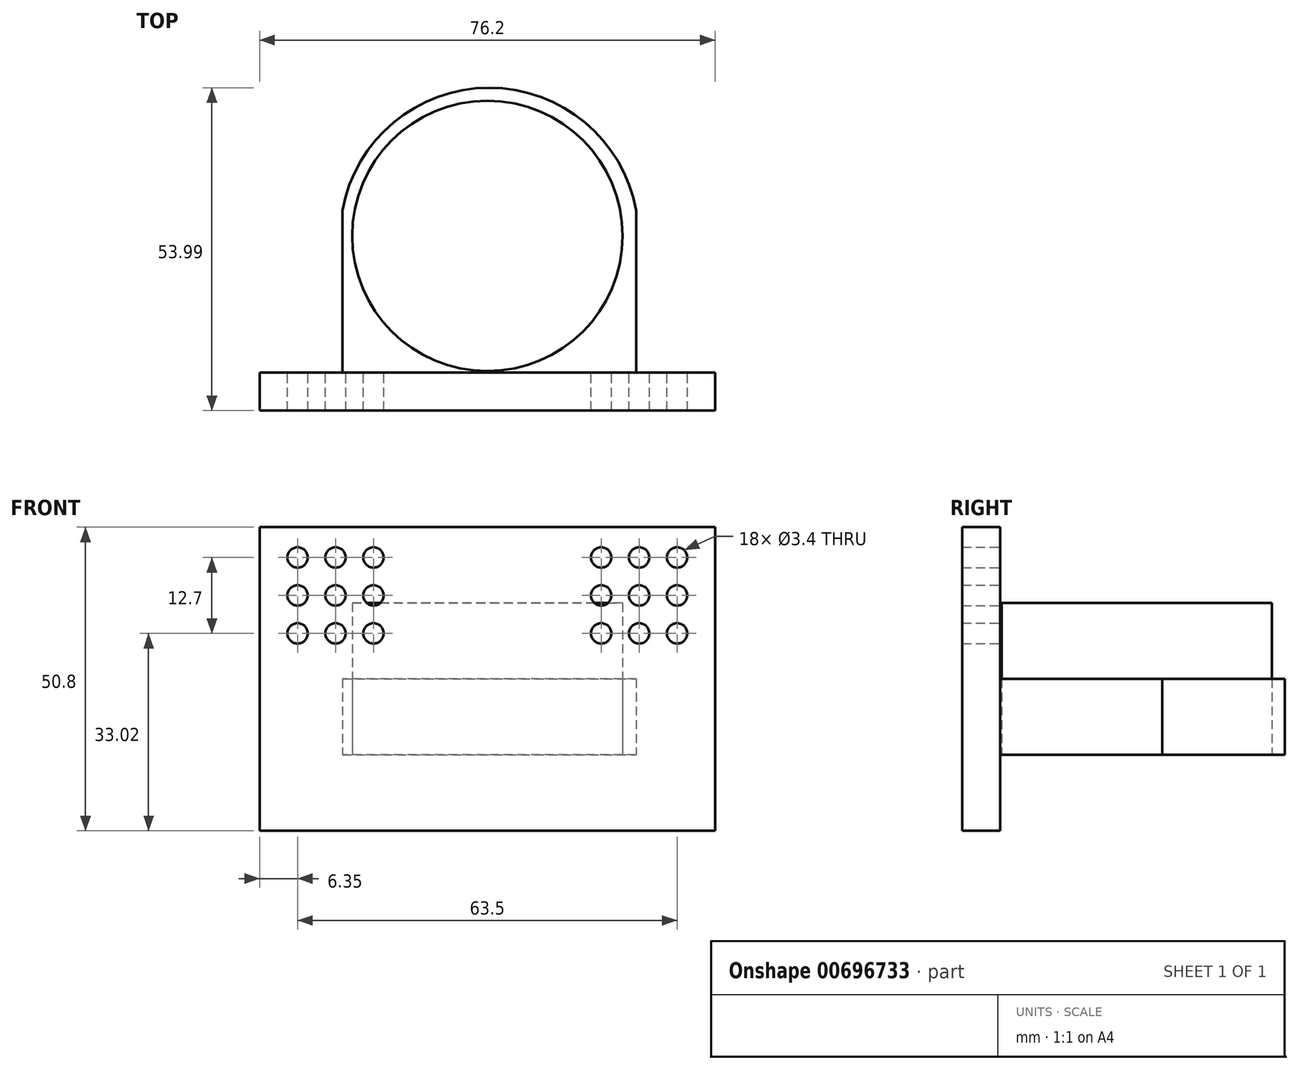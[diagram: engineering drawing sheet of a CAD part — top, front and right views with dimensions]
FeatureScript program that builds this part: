
annotation { "Feature Type Name" : "Feature", "Feature Type Description" : "" }
export const myFeature = defineFeature(function(context is Context, id is Id, definition is map)
    precondition{}
    {
        {
            var Q0;
            Q0=qCreatedBy(makeId("Top.planeOp"),FACE);
            var sketch = newSketch(context, id + "F0", { "sketchPlane" : qUnion([Q0])});
            skCircle(sketch, "E0", {"center": v(0, 0) * mm, "radius": 22.62 * mm});
            skSolve(sketch);
        }
        {
            var Q0;
            Q0=makeQuery(id+"F0.imprint","IMPRINT",FACE,{"disambiguationData":[TD([[makeQuery(id+"F0.imprint","IMPRINT",EDGE,{"derivedFrom":sQuery(id+"F0.wireOp",EDGE,"E0")}),1.0]])]});
            extrude(context, id + "F1", {"entities" : qUnion([Q0]), "depth" : 25.4 * mm, "offsetDistance" : 25.4 * mm});
        }
        {
            var Q0;
            Q0=qCreatedBy(makeId("Front.planeOp"),FACE);
            cPlane(context, id + "F2", {"entities" : qUnion([Q0]), "cplaneType" : CPlaneType.OFFSET, "offset" : 22.86 * mm, "width" : 152.4 * mm, "height" : 152.4 * mm});
        }
        {
            var Q0;
            Q0=qCreatedBy(id+"F2.planeOp",FACE);
            var sketch = newSketch(context, id + "F3", { "sketchPlane" : qUnion([Q0])});
            skLineSegment(sketch, "E1", {"start": v(-38.1, 38.1) * mm, "end": v(-38.1, -12.7) * mm});
            skLineSegment(sketch, "E2", {"start": v(-38.1, -12.7) * mm, "end": v(38.1, -12.7) * mm});
            skLineSegment(sketch, "E3", {"start": v(38.1, -12.7) * mm, "end": v(38.1, 38.1) * mm});
            skLineSegment(sketch, "E4", {"start": v(38.1, 38.1) * mm, "end": v(-38.1, 38.1) * mm});
            skLineSegment(sketch, "E5", {"start": v(22.62, 25.4) * mm, "end": v(22.62, 0) * mm});
            skLineSegment(sketch, "E6", {"start": v(-22.62, 0) * mm, "end": v(-22.62, 25.4) * mm});
            skCircle(sketch, "E7", {"center": v(31.75, 33.02) * mm, "radius": 1.7 * mm});
            skLineSegment(sketch, "E8", {"start": v(0, 38.1) * mm, "end": v(0, 23.2) * mm, "construction": true});
            skCircle(sketch, "E9.0.1.0", {"center": v(31.75, 26.67) * mm, "radius": 1.7 * mm});
            skCircle(sketch, "E9.0.2.0", {"center": v(31.75, 20.32) * mm, "radius": 1.7 * mm});
            skCircle(sketch, "E9.1.0.0", {"center": v(25.4, 33.02) * mm, "radius": 1.7 * mm});
            skCircle(sketch, "E9.1.1.0", {"center": v(25.4, 26.67) * mm, "radius": 1.7 * mm});
            skCircle(sketch, "E9.1.2.0", {"center": v(25.4, 20.32) * mm, "radius": 1.7 * mm});
            skCircle(sketch, "E9.2.0.0", {"center": v(19.05, 33.02) * mm, "radius": 1.7 * mm});
            skCircle(sketch, "E9.2.1.0", {"center": v(19.05, 26.67) * mm, "radius": 1.7 * mm});
            skCircle(sketch, "E9.2.2.0", {"center": v(19.05, 20.32) * mm, "radius": 1.7 * mm});
            skLineSegment(sketch, "E9.direction1", {"start": v(31.75, 33.02) * mm, "end": v(25.4, 33.02) * mm, "construction": true});
            skLineSegment(sketch, "E9.direction2", {"start": v(31.75, 33.02) * mm, "end": v(31.75, 26.67) * mm, "construction": true});
            skCircle(sketch, "E10.MirrorC", {"center": v(-31.75, 33.02) * mm, "radius": 1.7 * mm});
            skCircle(sketch, "E11.MirrorC", {"center": v(-25.4, 33.02) * mm, "radius": 1.7 * mm});
            skCircle(sketch, "E12.MirrorC", {"center": v(-19.05, 33.02) * mm, "radius": 1.7 * mm});
            skCircle(sketch, "E13.MirrorC", {"center": v(-19.05, 26.67) * mm, "radius": 1.7 * mm});
            skCircle(sketch, "E14.MirrorC", {"center": v(-25.4, 26.67) * mm, "radius": 1.7 * mm});
            skCircle(sketch, "E15.MirrorC", {"center": v(-31.75, 26.67) * mm, "radius": 1.7 * mm});
            skCircle(sketch, "E16.MirrorC", {"center": v(-31.75, 20.32) * mm, "radius": 1.7 * mm});
            skCircle(sketch, "E17.MirrorC", {"center": v(-25.4, 20.32) * mm, "radius": 1.7 * mm});
            skCircle(sketch, "E18.MirrorC", {"center": v(-19.05, 20.32) * mm, "radius": 1.7 * mm});
            skSolve(sketch);
        }
        {
            var Q0;
            Q0=makeQuery(id+"F3.imprint","IMPRINT",FACE,{"disambiguationData":[TD([[makeQuery(id+"F3.imprint","IMPRINT",EDGE,{"derivedFrom":sQuery(id+"F3.wireOp",EDGE,"E1")}),1.0]])]});
            extrude(context, id + "F4", {"entities" : qUnion([Q0]), "depth" : 6.35 * mm, "offsetDistance" : 25.4 * mm});
        }
        {
            var Q0;
            Q0=qCreatedBy(makeId("Top.planeOp"),FACE);
            var sketch = newSketch(context, id + "F5", { "sketchPlane" : qUnion([Q0])});
            skCircle(sketch, "E19.0", {"center": v(0, 0) * mm, "radius": 22.62 * mm});
            skLineSegment(sketch, "E20.0", {"start": v(-38.1, -22.86) * mm, "end": v(38.1, -22.86) * mm});
            skLineSegment(sketch, "E21", {"start": v(-24.25, -22.86) * mm, "end": v(-24.25, 4.27) * mm});
            skLineSegment(sketch, "E22", {"start": v(24.89, 4.27) * mm, "end": v(24.89, -22.86) * mm});
            skArc(sketch, "E23", {"start": v(24.89, 4.27) * mm, "mid": v(0.32, 24.78) * mm, "end": v(-24.25, 4.27) * mm});
            skPoint(sketch, "E24.start.orphan", {"position": v(-24.25, 31.4) * mm});
            skPoint(sketch, "E25.orphan", {"position": v(24.89, 31.4) * mm});
            skSolve(sketch);
        }
        {
            var Q0;
            Q0=makeQuery(id+"F5.imprint","IMPRINT",FACE,{"disambiguationData":[TD([[makeQuery(id+"F5.imprint","IMPRINT",EDGE,{"derivedFrom":sQuery(id+"F5.wireOp",EDGE,"E19.0")}),-1.0]])]});
            extrude(context, id + "F6", {"entities" : qUnion([Q0]), "depth" : 12.7 * mm, "offsetDistance" : 25.4 * mm});
        }
    });
